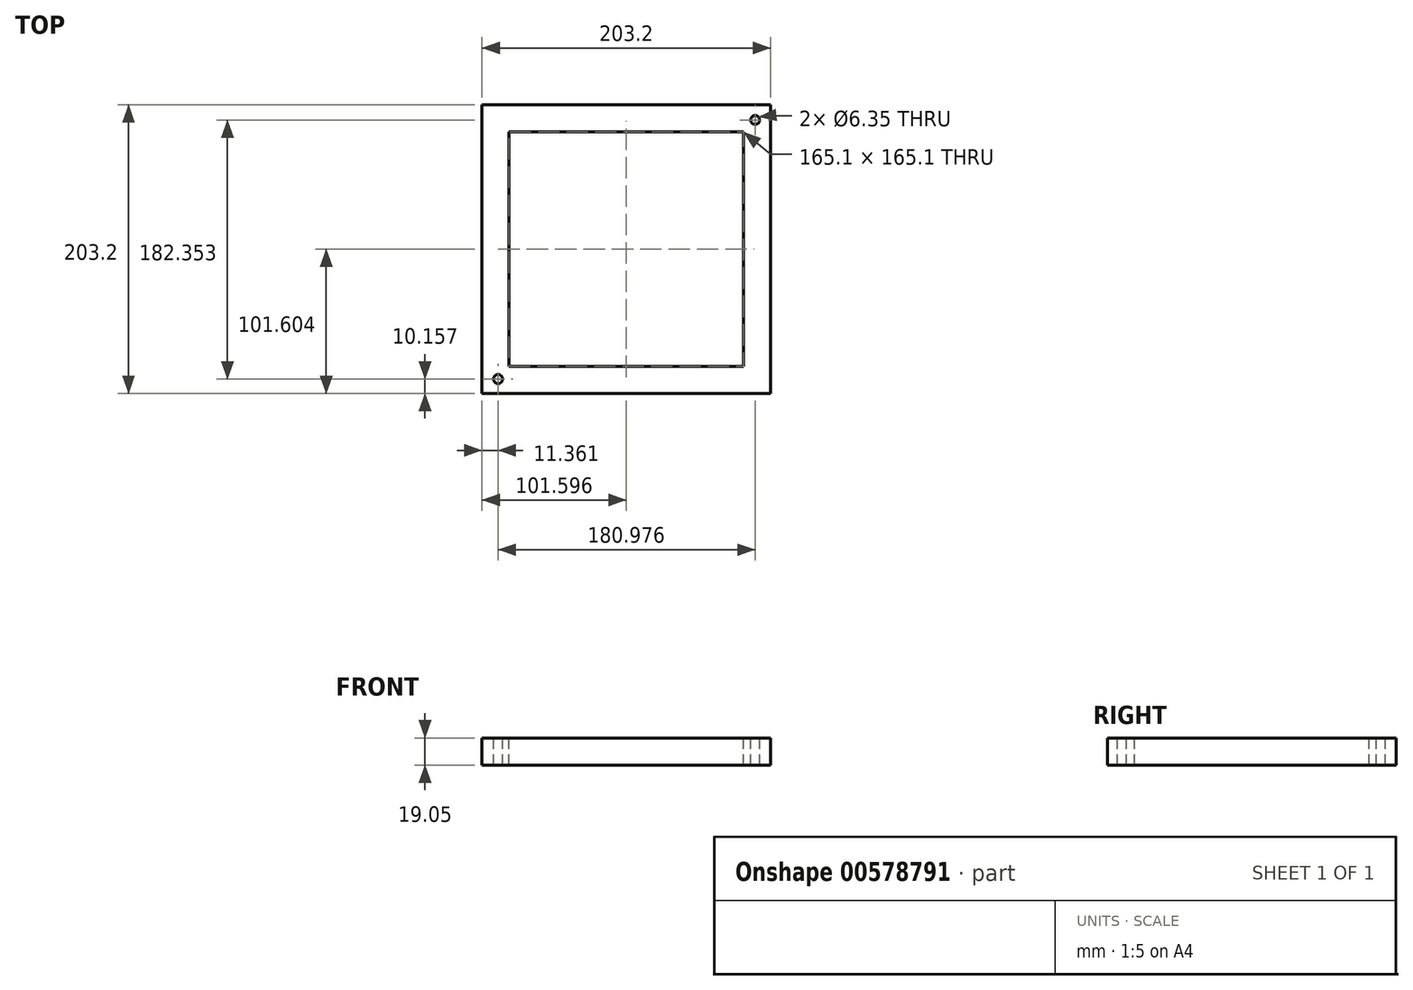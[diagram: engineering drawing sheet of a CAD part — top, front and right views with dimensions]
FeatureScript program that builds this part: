
annotation { "Feature Type Name" : "Feature", "Feature Type Description" : "" }
export const myFeature = defineFeature(function(context is Context, id is Id, definition is map)
    precondition{}
    {
        {
            var Q0;
            Q0=qCreatedBy(makeId("Top.planeOp"),FACE);
            var sketch = newSketch(context, id + "F0", { "sketchPlane" : qUnion([Q0])});
            skLineSegment(sketch, "E0.bottom", {"start": v(-121.86, 138.73) * mm, "end": v(81.34, 138.73) * mm});
            skLineSegment(sketch, "E0.top", {"start": v(-121.86, -64.47) * mm, "end": v(81.34, -64.47) * mm});
            skLineSegment(sketch, "E0.left", {"start": v(-121.86, 138.73) * mm, "end": v(-121.86, -64.47) * mm});
            skLineSegment(sketch, "E0.right", {"start": v(81.34, 138.73) * mm, "end": v(81.34, -64.47) * mm});
            skSolve(sketch);
        }
        {
            var Q0;
            Q0=makeQuery(id+"F0.imprint","IMPRINT",FACE,{"disambiguationData":[TD([[makeQuery(id+"F0.imprint","IMPRINT",EDGE,{"derivedFrom":sQuery(id+"F0.wireOp",EDGE,"E0.bottom")}),-1.0]])]});
            extrude(context, id + "F1", {"entities" : qUnion([Q0]), "depth" : 19.05 * mm, "offsetDistance" : 25.4 * mm});
        }
        {
            var Q0;
            Q0=makeQuery(id+"F1.opExtrude","CAP_FACE",FACE,{"disambiguationData":[OSD([sQuery(id+"F0.wireOp",EDGE,"E0.bottom"),sQuery(id+"F0.wireOp",EDGE,"E0.top"),sQuery(id+"F0.wireOp",EDGE,"E0.left"),sQuery(id+"F0.wireOp",EDGE,"E0.right")])],"isStart":false});
            var sketch = newSketch(context, id + "F2", { "sketchPlane" : qUnion([Q0])});
            skLineSegment(sketch, "E1", {"start": v(-121.86, 138.73) * mm, "end": v(-102.81, 138.73) * mm});
            skLineSegment(sketch, "E2", {"start": v(-102.81, 138.73) * mm, "end": v(-102.81, -64.47) * mm});
            skLineSegment(sketch, "E3", {"start": v(81.34, -64.47) * mm, "end": v(62.29, -64.47) * mm});
            skLineSegment(sketch, "E4", {"start": v(62.29, -64.47) * mm, "end": v(62.29, 138.73) * mm});
            skLineSegment(sketch, "E5", {"start": v(81.34, 138.73) * mm, "end": v(81.34, 119.68) * mm});
            skLineSegment(sketch, "E6", {"start": v(81.34, 119.68) * mm, "end": v(-121.86, 119.68) * mm});
            skLineSegment(sketch, "E7", {"start": v(-121.86, -64.47) * mm, "end": v(-121.86, -45.42) * mm});
            skLineSegment(sketch, "E8", {"start": v(-121.86, -45.42) * mm, "end": v(81.34, -45.42) * mm});
            skSolve(sketch);
        }
        {
            var Q0;
            {var subQ0=sQuery(id+"F2.wireOp",EDGE,"E6");var subQ1=sQuery(id+"F2.wireOp",EDGE,"E2");var subQ2=makeQuery(id+"F2.imprint","INTERSECT",VERTEX,{"derivedFrom":[subQ1,subQ0]});Q0=makeQuery(id+"F2.imprint","IMPRINT",FACE,{"disambiguationData":[TD([[makeQuery(id+"F2.imprint","IMPRINT",EDGE,{"disambiguationData":[TD([[subQ2,-1.0]])],"derivedFrom":subQ1}),1.0]])]});}
            extrude(context, id + "F3", {"entities" : qUnion([Q0]), "operationType" : NewBodyOperationType.REMOVE, "endBound" : BoundingType.THROUGH_ALL, "oppositeDirection" : true, "depth" : 25.4 * mm, "offsetDistance" : 25.4 * mm});
        }
        {
            var Q0;
            Q0=makeQuery(id+"F1.opExtrude","CAP_FACE",FACE,{"disambiguationData":[OSD([sQuery(id+"F0.wireOp",EDGE,"E0.bottom"),sQuery(id+"F0.wireOp",EDGE,"E0.top"),sQuery(id+"F0.wireOp",EDGE,"E0.left"),sQuery(id+"F0.wireOp",EDGE,"E0.right")])],"isStart":false});
            var sketch = newSketch(context, id + "F4", { "sketchPlane" : qUnion([Q0])});
            skLineSegment(sketch, "E9", {"start": v(-121.86, -64.47) * mm, "end": v(-110.5, -54.31) * mm});
            skCircle(sketch, "E10", {"center": v(-110.5, -54.31) * mm, "radius": 3.18 * mm});
            skLineSegment(sketch, "E11", {"start": v(81.34, 138.73) * mm, "end": v(70.48, 128.04) * mm});
            skCircle(sketch, "E12", {"center": v(70.48, 128.04) * mm, "radius": 3.18 * mm});
            skSolve(sketch);
        }
        {
            var Q0;
            Q0=makeQuery(id+"F4.imprint","IMPRINT",FACE,{"disambiguationData":[TD([[makeQuery(id+"F4.imprint","IMPRINT",EDGE,{"derivedFrom":sQuery(id+"F4.wireOp",EDGE,"E10")}),1.0]])]});
            var Q1;
            Q1=makeQuery(id+"F4.imprint","IMPRINT",FACE,{"disambiguationData":[TD([[makeQuery(id+"F4.imprint","IMPRINT",EDGE,{"derivedFrom":sQuery(id+"F4.wireOp",EDGE,"E12")}),1.0]])]});
            extrude(context, id + "F5", {"entities" : qUnion([Q0, Q1]), "operationType" : NewBodyOperationType.REMOVE, "endBound" : BoundingType.THROUGH_ALL, "oppositeDirection" : true, "depth" : 25.4 * mm, "offsetDistance" : 25.4 * mm});
        }
    });
